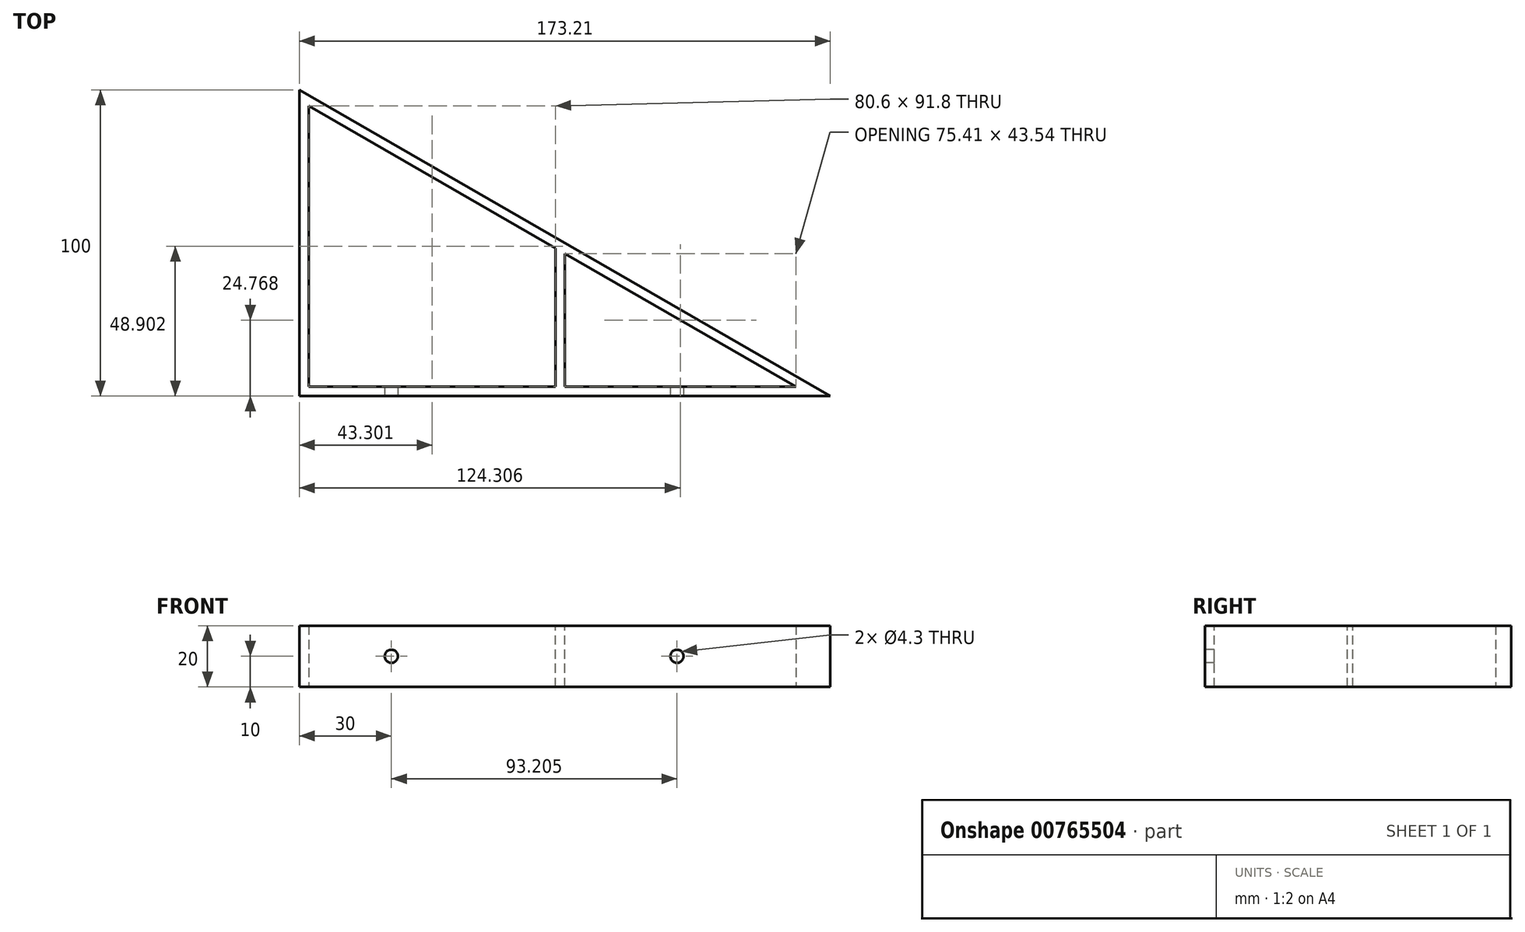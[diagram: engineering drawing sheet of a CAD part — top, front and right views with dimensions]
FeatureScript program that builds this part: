
annotation { "Feature Type Name" : "Feature", "Feature Type Description" : "" }
export const myFeature = defineFeature(function(context is Context, id is Id, definition is map)
    precondition{}
    {
        {
            var Q0;
            Q0=qCreatedBy(makeId("Top.planeOp"),FACE);
            var sketch = newSketch(context, id + "F0", { "sketchPlane" : qUnion([Q0])});
            skLineSegment(sketch, "E0", {"start": v(0, 0) * mm, "end": v(0, 100) * mm});
            skLineSegment(sketch, "E1", {"start": v(0, 100) * mm, "end": v(173.2, 0) * mm});
            skLineSegment(sketch, "E2", {"start": v(173.2, 0) * mm, "end": v(0, 0) * mm});
            skSolve(sketch);
        }
        {
            var Q0;
            Q0=makeQuery(id+"F0.imprint","IMPRINT",FACE,{"disambiguationData":[TD([[makeQuery(id+"F0.imprint","IMPRINT",EDGE,{"derivedFrom":sQuery(id+"F0.wireOp",EDGE,"E0")}),-1.0]])]});
            extrude(context, id + "F1", {"entities" : qUnion([Q0]), "depth" : 20 * mm, "offsetDistance" : 25.4 * mm});
        }
        {
            var Q0;
            Q0=makeQuery(id+"F1.opExtrude","CAP_FACE",FACE,{"disambiguationData":[OSD([sQuery(id+"F0.wireOp",EDGE,"E0"),sQuery(id+"F0.wireOp",EDGE,"E1"),sQuery(id+"F0.wireOp",EDGE,"E2")])],"isStart":false});
            var Q1;
            Q1=makeQuery(id+"F1.opExtrude","CAP_FACE",FACE,{"disambiguationData":[OSD([sQuery(id+"F0.wireOp",EDGE,"E0"),sQuery(id+"F0.wireOp",EDGE,"E1"),sQuery(id+"F0.wireOp",EDGE,"E2")])],"isStart":true});
            shell(context, id + "F2", {"entities" : qUnion([Q0, Q1]), "thickness" : 3 * mm});
        }
        {
            var Q0;
            Q0=makeQuery(id+"F1.opExtrude","CAP_FACE",FACE,{"disambiguationData":[OSD([sQuery(id+"F0.wireOp",EDGE,"E0"),sQuery(id+"F0.wireOp",EDGE,"E1"),sQuery(id+"F0.wireOp",EDGE,"E2")])],"isStart":false});
            var sketch = newSketch(context, id + "F3", { "sketchPlane" : qUnion([Q0])});
            skLineSegment(sketch, "E3.bottom", {"start": v(86.6, 50) * mm, "end": v(83.6, 50) * mm});
            skLineSegment(sketch, "E3.top", {"start": v(86.6, 0) * mm, "end": v(83.6, 0) * mm});
            skLineSegment(sketch, "E3.left", {"start": v(86.6, 50) * mm, "end": v(86.6, 0) * mm});
            skLineSegment(sketch, "E3.right", {"start": v(83.6, 50) * mm, "end": v(83.6, 0) * mm});
            skSolve(sketch);
        }
        {
            var Q0;
            {var subQ0=sQuery(id+"F3.wireOp",EDGE,"E3.left");var subQ1=sQuery(id+"F0.wireOp",EDGE,"E1");var subQ2=makeQuery(id+"F2.opShell","OFFSET_EDGE",EDGE,{"disambiguationData":[OSD([subQ1]),TDD([makeQuery(id+"F1.opExtrude","CAP_EDGE",EDGE,{"disambiguationData":[OSD([subQ1])],"isStart":false})])]});var subQ3=makeQuery(id+"F3.imprint","INTERSECT",VERTEX,{"derivedFrom":[subQ2,subQ0]});Q0=makeQuery(id+"F3.imprint","IMPRINT",FACE,{"disambiguationData":[TD([[makeQuery(id+"F3.imprint","IMPRINT",EDGE,{"disambiguationData":[TD([[subQ3,-1.0]])],"derivedFrom":subQ0}),-1.0]])]});}
            extrude(context, id + "F4", {"entities" : qUnion([Q0]), "operationType" : NewBodyOperationType.ADD, "oppositeDirection" : true, "depth" : 20 * mm, "offsetDistance" : 25.4 * mm});
        }
        {
            var Q0;
            Q0=qCreatedBy(makeId("Front.planeOp"),FACE);
            var sketch = newSketch(context, id + "F5", { "sketchPlane" : qUnion([Q0])});
            skPoint(sketch, "E4", {"position": v(30, 10) * mm});
            skPoint(sketch, "E5", {"position": v(123.2, 10) * mm});
            skSolve(sketch);
        }
        {
            var Q0;
            Q0=sQuery(id+"F5.wireOp",VERTEX,"E4");
            var Q1;
            Q1=sQuery(id+"F5.wireOp",VERTEX,"E5");
            var Q2;
            Q2=makeQuery(id+"F1.opExtrude","SWEPT_BODY",BODY,{"disambiguationData":[OSD([sQuery(id+"F0.wireOp",EDGE,"E0"),sQuery(id+"F0.wireOp",EDGE,"E1"),sQuery(id+"F0.wireOp",EDGE,"E2")])]});
            hole(context, id + "F6", {"style" : HoleStyle.SIMPLE, "endStyle" : HoleEndStyle.BLIND, "holeDiameter" : 4.3 * mm, "majorDiameter" : 6.35 * mm, "holeDepth" : 5 * mm, "isTappedThrough" : true, "tappedDepth" : 12.7 * mm, "tapClearance" : 3, "locations" : qUnion([Q0, Q1]), "scope" : qUnion([Q2])});
        }
    });
